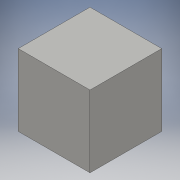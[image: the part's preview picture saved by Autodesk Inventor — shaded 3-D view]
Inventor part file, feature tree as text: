
AUTODESK INVENTOR PART (.ipt)
format: ipt  version: 2016 (Build 200138000, 138)  size: 84,992 bytes
history: native  units: in
note: dims shown in document units (in); Inventor stores cm internally (conversion verified against a paired STEP export)
features: extrude x1, sketch x1
ambient origin geometry x8: Origin, YZ Plane, XZ Plane, XY Plane, X Axis, Y Axis, Z Axis, Center Point
bodies: Body1 (feature_tree)
feature tree (2):
  extrude  "Extrusion2"  Depth=1.9685in
  sketch  "Sketch2"  dims[d4=1.9685in d5=1.9685in d6=1.9685in d7=0.0in]
